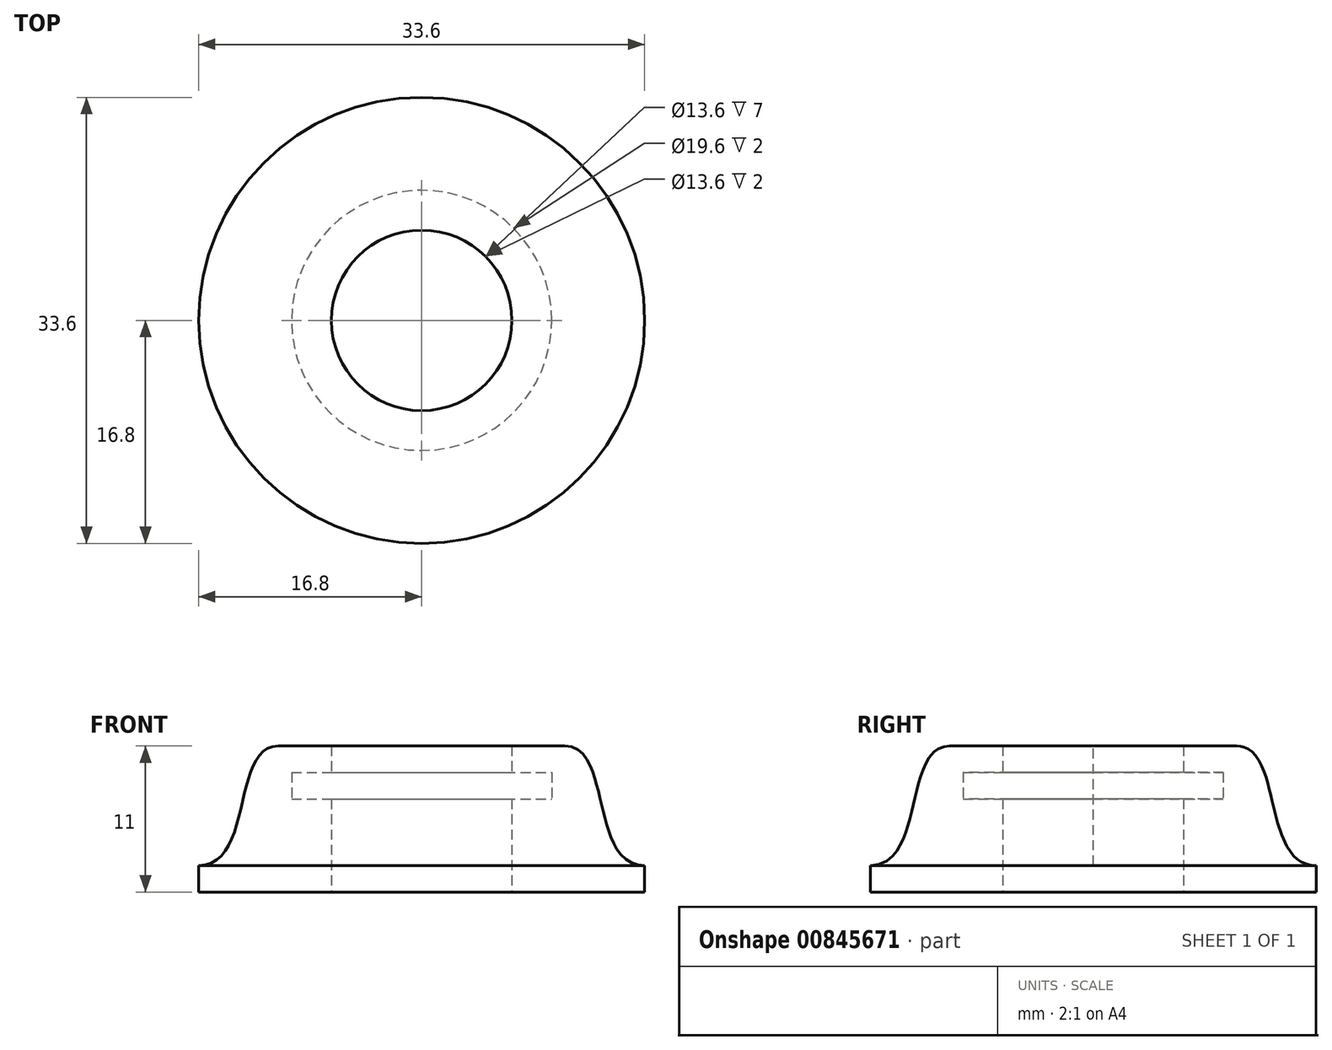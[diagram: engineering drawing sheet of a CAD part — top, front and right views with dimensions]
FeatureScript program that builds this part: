
annotation { "Feature Type Name" : "Feature", "Feature Type Description" : "" }
export const myFeature = defineFeature(function(context is Context, id is Id, definition is map)
    precondition{}
    {
        {
            var Q0;
            Q0=qCreatedBy(makeId("Front.planeOp"),FACE);
            var sketch = newSketch(context, id + "F0", { "sketchPlane" : qUnion([Q0])});
            skLineSegment(sketch, "E0.bottom", {"start": v(-6.8, 0) * mm, "end": v(-16.8, 0) * mm});
            skLineSegment(sketch, "E0.top", {"start": v(-6.8, 2) * mm, "end": v(-16.8, 2) * mm});
            skLineSegment(sketch, "E0.left", {"start": v(-6.8, 0) * mm, "end": v(-6.8, 2) * mm});
            skLineSegment(sketch, "E0.right", {"start": v(-16.8, 0) * mm, "end": v(-16.8, 2) * mm});
            skLineSegment(sketch, "E1.bottom", {"start": v(-6.8, 2) * mm, "end": v(-10.8, 2) * mm});
            skLineSegment(sketch, "E1.top", {"start": v(-6.8, 7) * mm, "end": v(-10.8, 7) * mm});
            skLineSegment(sketch, "E1.left", {"start": v(-6.8, 2) * mm, "end": v(-6.8, 7) * mm});
            skLineSegment(sketch, "E1.right", {"start": v(-10.8, 2) * mm, "end": v(-10.8, 7) * mm});
            skLineSegment(sketch, "E2.bottom", {"start": v(-10.8, 7) * mm, "end": v(-9.8, 7) * mm});
            skLineSegment(sketch, "E2.top", {"start": v(-10.8, 9) * mm, "end": v(-9.8, 9) * mm});
            skLineSegment(sketch, "E2.left", {"start": v(-10.8, 7) * mm, "end": v(-10.8, 9) * mm});
            skLineSegment(sketch, "E2.right", {"start": v(-9.8, 7) * mm, "end": v(-9.8, 9) * mm});
            skLineSegment(sketch, "E3.bottom", {"start": v(-10.8, 9) * mm, "end": v(-6.8, 9) * mm});
            skLineSegment(sketch, "E3.top", {"start": v(-10.8, 11) * mm, "end": v(-6.8, 11) * mm});
            skLineSegment(sketch, "E3.left", {"start": v(-10.8, 9) * mm, "end": v(-10.8, 11) * mm});
            skLineSegment(sketch, "E3.right", {"start": v(-6.8, 9) * mm, "end": v(-6.8, 11) * mm});
            skFitSpline(sketch, "E4", {"points": [v(-16.8, 2) * mm, v(-10.8, 11) * mm], "startDerivative": vector(12.51, 0) * mm, "endDerivative": vector(10.69, 0) * mm});
            skLineSegment(sketch, "E5", {"start": v(0, 0) * mm, "end": v(0, 5.4) * mm});
            skSolve(sketch);
        }
        {
            var Q0;
            Q0=makeQuery(id+"F0.imprint","IMPRINT",FACE,{"disambiguationData":[TD([[makeQuery(id+"F0.imprint","IMPRINT",EDGE,{"derivedFrom":sQuery(id+"F0.wireOp",EDGE,"E2.top")}),1.0]])]});
            var Q1;
            Q1=makeQuery(id+"F0.imprint","IMPRINT",FACE,{"disambiguationData":[TD([[makeQuery(id+"F0.imprint","IMPRINT",EDGE,{"derivedFrom":sQuery(id+"F0.wireOp",EDGE,"E2.top")}),-1.0]])]});
            var Q2;
            {var subQ0=sQuery(id+"F0.wireOp",EDGE,"E1.right");Q2=makeQuery(id+"F0.imprint","IMPRINT",FACE,{"disambiguationData":[TD([[makeQuery(id+"F0.imprint","IMPRINT",EDGE,{"derivedFrom":subQ0}),1.0]])]});}
            var Q3;
            {var subQ2=sQuery(id+"F0.wireOp",EDGE,"E1.left");Q3=makeQuery(id+"F0.imprint","IMPRINT",FACE,{"disambiguationData":[TD([[makeQuery(id+"F0.imprint","IMPRINT",EDGE,{"derivedFrom":subQ2}),1.0]])]});}
            var Q4;
            Q4=makeQuery(id+"F0.imprint","IMPRINT",FACE,{"disambiguationData":[TD([[makeQuery(id+"F0.imprint","IMPRINT",EDGE,{"derivedFrom":sQuery(id+"F0.wireOp",EDGE,"E0.bottom")}),-1.0]])]});
            var Q5;
            Q5=makeQuery(id+"F0.imprint","IMPRINT",FACE,{"disambiguationData":[TD([[makeQuery(id+"F0.imprint","IMPRINT",EDGE,{"derivedFrom":sQuery(id+"F0.wireOp",EDGE,"E0.right")}),1.0]])]});
            var Q6;
            Q6=sQuery(id+"F0.wireOp",EDGE,"E5");
            revolve(context, id + "F1", {"surfaceOperationType" : NewSurfaceOperationType.NEW, "entities" : qUnion([Q0, Q1, Q2, Q3, Q4, Q5]), "axis" : qUnion([Q6]), "revolveType" : RevolveType.FULL});
        }
    });
